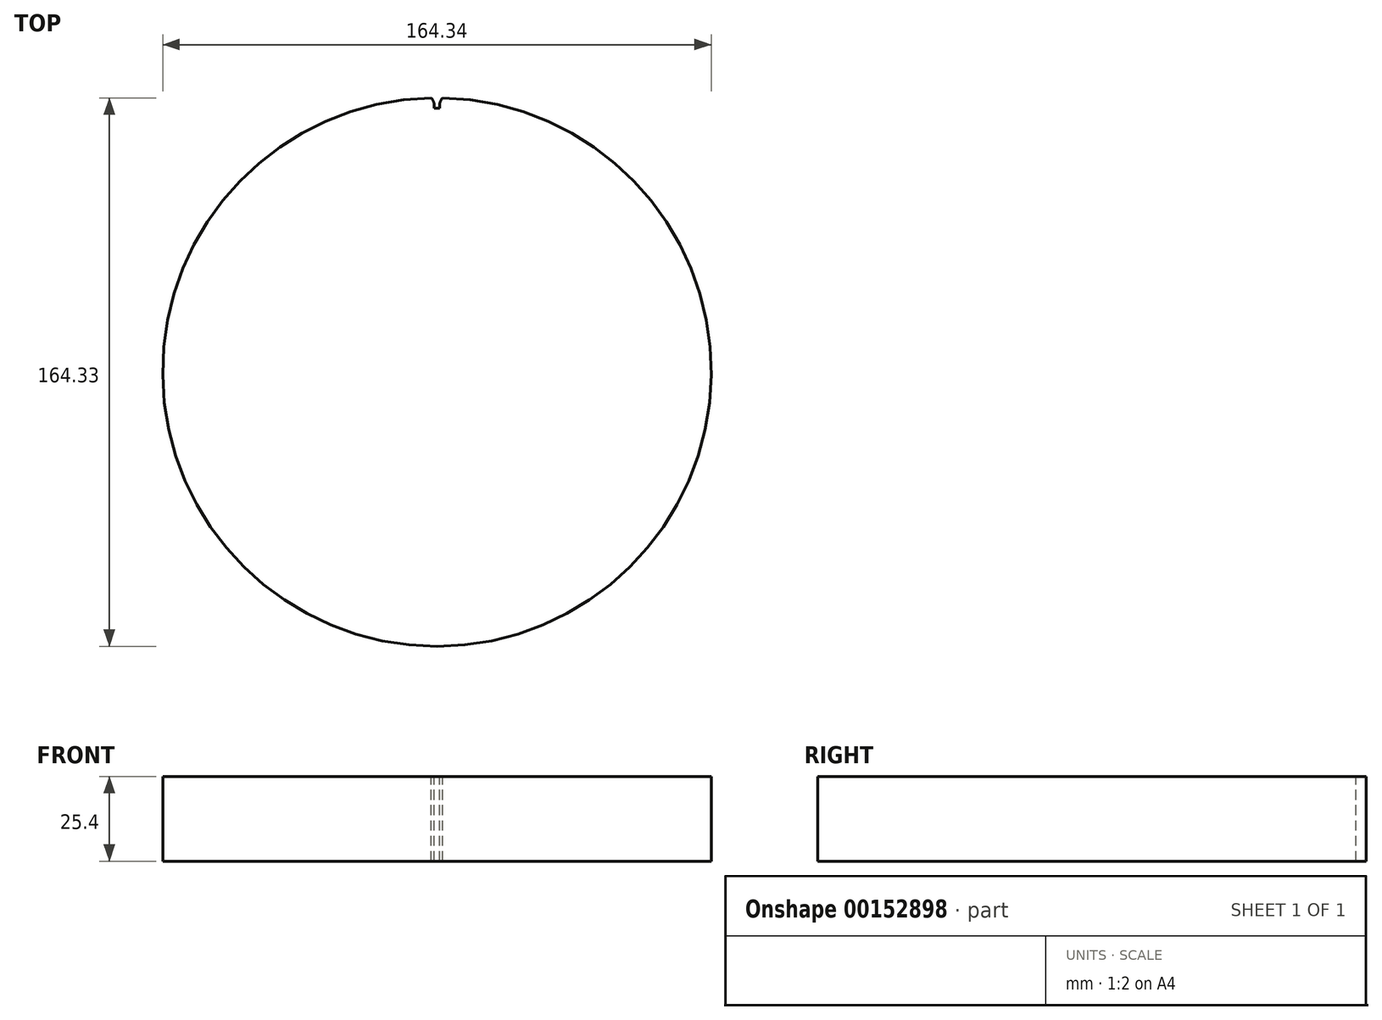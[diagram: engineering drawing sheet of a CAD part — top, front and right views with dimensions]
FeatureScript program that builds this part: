
annotation { "Feature Type Name" : "Feature", "Feature Type Description" : "" }
export const myFeature = defineFeature(function(context is Context, id is Id, definition is map)
    precondition{}
    {
        {
            var Q0;
            Q0=qCreatedBy(makeId("Top.planeOp"),FACE);
            var sketch = newSketch(context, id + "F0", { "sketchPlane" : qUnion([Q0])});
            skCircle(sketch, "E0", {"center": v(0, 0) * mm, "radius": 82.17 * mm});
            skSolve(sketch);
        }
        {
            var Q0;
            Q0 = qSketchRegion(id + "F0", true);
            extrude(context, id + "F1", {"entities" : qUnion([Q0]), "depth" : 25.4 * mm});
        }
        {
            var Q0;
            Q0=makeQuery(id+"F1.opExtrude","CAP_FACE",FACE,{"disambiguationData":[OSD([sQuery(id+"F0.wireOp",EDGE,"E0")])],"isStart":false});
            var sketch = newSketch(context, id + "F2", { "sketchPlane" : qUnion([Q0])});
            skLineSegment(sketch, "E1", {"start": v(-1.7, 82.16) * mm, "end": v(-0.8, 79.8) * mm, "construction": true});
            skLineSegment(sketch, "E2", {"start": v(0, 0) * mm, "end": v(0, 79) * mm, "construction": true});
            skLineSegment(sketch, "E3.top", {"start": v(-0.8, 79) * mm, "end": v(0.8, 79) * mm});
            skLineSegment(sketch, "E3.left", {"start": v(-0.8, 79.8) * mm, "end": v(-0.8, 79) * mm});
            skLineSegment(sketch, "E3.right", {"start": v(0.8, 79.8) * mm, "end": v(0.8, 79) * mm});
            skLineSegment(sketch, "E4", {"start": v(-0.8, 79.8) * mm, "end": v(0, 79.8) * mm, "construction": true});
            skLineSegment(sketch, "E5", {"start": v(0, 79.8) * mm, "end": v(0.8, 79.8) * mm, "construction": true});
            skArc(sketch, "E6", {"start": v(-0.8, 79.8) * mm, "mid": v(-1.03, 81.06) * mm, "end": v(-1.7, 82.16) * mm});
            skArc(sketch, "E7", {"start": v(1.7, 82.16) * mm, "mid": v(1.03, 81.06) * mm, "end": v(0.8, 79.8) * mm});
            skArc(sketch, "E8", {"start": v(1.7, 82.16) * mm, "mid": v(0, 82.17) * mm, "end": v(-1.7, 82.16) * mm});
            skLineSegment(sketch, "E9", {"start": v(0.8, 79.8) * mm, "end": v(1.7, 82.16) * mm, "construction": true});
            skLineSegment(sketch, "E10", {"start": v(-1.26, 82.16) * mm, "end": v(0, 0) * mm, "construction": true});
            skPoint(sketch, "E11", {"position": v(-1.24, 80.97) * mm});
            skLineSegment(sketch, "E12", {"start": v(0, 79) * mm, "end": v(0, 82.17) * mm, "construction": true});
            skLineSegment(sketch, "E13", {"start": v(0, 0) * mm, "end": v(4.4, 78.88) * mm, "construction": true});
            skLineSegment(sketch, "E14", {"start": v(4.4, 78.88) * mm, "end": v(4.58, 82.05) * mm, "construction": true});
            skLineSegment(sketch, "E15.bottom", {"start": v(3.6, 78.92) * mm, "end": v(5.2, 78.83) * mm, "construction": true});
            skLineSegment(sketch, "E15.top", {"start": v(3.65, 79.71) * mm, "end": v(5.24, 79.62) * mm, "construction": true});
            skLineSegment(sketch, "E15.left", {"start": v(3.6, 78.92) * mm, "end": v(3.65, 79.71) * mm, "construction": true});
            skLineSegment(sketch, "E15.right", {"start": v(5.2, 78.83) * mm, "end": v(5.24, 79.62) * mm, "construction": true});
            skLineSegment(sketch, "E16", {"start": v(3.65, 79.71) * mm, "end": v(2.89, 82.12) * mm, "construction": true});
            skArc(sketch, "E17", {"start": v(3.65, 79.71) * mm, "mid": v(3.5, 80.99) * mm, "end": v(2.89, 82.12) * mm, "construction": true});
            skArc(sketch, "E18", {"start": v(6.27, 81.93) * mm, "mid": v(5.54, 80.87) * mm, "end": v(5.24, 79.62) * mm, "construction": true});
            skLineSegment(sketch, "E19", {"start": v(5.24, 79.62) * mm, "end": v(6.27, 81.93) * mm, "construction": true});
            skArc(sketch, "E20", {"start": v(6.27, 81.93) * mm, "mid": v(4.58, 82.05) * mm, "end": v(2.89, 82.12) * mm, "construction": true});
            skLineSegment(sketch, "E21", {"start": v(1.7, 82.16) * mm, "end": v(2.89, 82.12) * mm, "construction": true});
            skSolve(sketch);
        }
        {
            var Q0;
            Q0 = qSketchRegion(id + "F2", true);
            var Q1;
            Q1=makeQuery(id+"F1.opExtrude","CAP_FACE",FACE,{"disambiguationData":[OSD([sQuery(id+"F0.wireOp",EDGE,"E0")])],"isStart":true});
            extrude(context, id + "F3", {"entities" : qUnion([Q0]), "operationType" : NewBodyOperationType.REMOVE, "endBound" : BoundingType.UP_TO_SURFACE, "oppositeDirection" : true, "endBoundEntityFace" : qUnion([Q1]), "depth" : 25.4 * mm});
        }
    });
